# Revit family: 7372 Указатель чугунный высокий арт_497 Хоббика
name_source: partatom
category: Антураж
revit_build: Autodesk Revit 2018 (Build: 20180423_1000(x64)
units: mm (PartAtom-declared; Revit-internal decimal feet)

## family parameters
Всегда вертикально = Да
Источник визуального образа = Геометрия семейства
На основе рабочей плоскости = Нет
Общий = Нет
При загрузке вырезать с полостями = Нет
Точка расчета площади = Нет

## types (3) — shared parameters
URL = https://hobbyka.ru
Артикул товара = Арт. 7372
Группа модели = Стенды и указатели
Длина = 800 мм
Изготовитель = ООО «Хоббика»
Изображение типоразмера = Указатель чугунный высокий арт_497 Арт 7372.jpg
Материал изделия = Чугун
Цвет каркаса = Чугун
Ширина = 235 мм

## per-type parameters (varying)
| type | Версия 2,5 м | Версия 3,0 м | Версия 3,5 м | Высота | Описание |
| Версия 3,5 м | Нет | Нет | Да | 3500 мм | Указатель чугунный высокий арт. 497. Версия 3,5 м |
| Версия 3,0 м | Нет | Да | Нет | 3000 мм | Указатель чугунный высокий арт. 497. Версия 3,0 м |
| Версия 2,5 м | Да | Нет | Нет | 2500 мм | Указатель чугунный высокий арт. 497. Версия 2,5 м |
